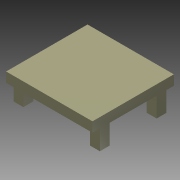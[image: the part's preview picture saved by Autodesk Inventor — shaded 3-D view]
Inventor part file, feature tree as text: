
AUTODESK INVENTOR PART (.ipt)
format: ipt  version: 2015 (Build 190159000, 159)  size: 480,256 bytes
history: native  units: in
note: dims shown in document units (in); Inventor stores cm internally (conversion verified against a paired STEP export)
features: thread x34, other x13, sketch x10, plane x6, projected_geometry x6, extrude x5, hole x4, mirror x3, pattern_circular x1, boolean_combine x1
ambient origin geometry x8: Origin, YZ Plane, XZ Plane, XY Plane, X Axis, Y Axis, Z Axis, Center Point
bodies: Solid6 (feature_tree)
feature tree (83):
  other  "board_with_hole_pipes.ipt"
  other  "Layout with const "
  plane  "Work Plane1"
  extrude  "Extrusion1"  Depth=18.0in
  extrude  "Extrusion2"  Depth=24.0in
  hole  "Hole1"  [1 undecoded]
  thread  "Thread1"  [1 undecoded]
  pattern_circular  "Circular Pattern1"  [2 undecoded]
  plane  "Work Plane3"
  hole  "Hole2"  [1 undecoded]
  thread  "Thread2"  [1 undecoded]
  thread  "Thread3"  [1 undecoded]
  thread  "Thread4"  [1 undecoded]
  thread  "Thread5"  [1 undecoded]
  thread  "Thread6"  [1 undecoded]
  thread  "Thread7"  [1 undecoded]
  mirror  "Mirror1"
  mirror  "Mirror2"
  mirror  "Mirror3"
  plane  "Work Plane4"
  extrude  "Extrusion3"  Depth=1.0in
  thread  "Thread8"  [1 undecoded]
  thread  "Thread9"  [1 undecoded]
  thread  "Thread10"  [1 undecoded]
  thread  "Thread11"  [1 undecoded]
  thread  "Thread12"  [1 undecoded]
  thread  "Thread13"  [1 undecoded]
  thread  "Thread14"  [1 undecoded]
  thread  "Thread15"  [1 undecoded]
  thread  "Thread16"  [1 undecoded]
  thread  "Thread17"  [1 undecoded]
  thread  "Thread18"  [1 undecoded]
  thread  "Thread19"  [1 undecoded]
  thread  "Thread20"  [1 undecoded]
  thread  "Thread21"  [1 undecoded]
  thread  "Thread22"  [1 undecoded]
  thread  "Thread23"  [1 undecoded]
  thread  "Thread24"  [1 undecoded]
  thread  "Thread25"  [1 undecoded]
  extrude  "Extrusion4"  Depth=1.0in TaperAngle=0.0deg
  plane  "Work Plane7"
  extrude  "Extrusion5"  Depth=1.0in TaperAngle=0.0deg
  boolean_combine  "Combine1"
  plane  "Work Plane8"
  plane  "Work Plane9"
  hole  "Hole3"  [1 undecoded]
  hole  "Hole4"  [1 undecoded]
  thread  "Thread26"  [1 undecoded]
  thread  "Thread27"  [1 undecoded]
  thread  "Thread28"  [1 undecoded]
  thread  "Thread29"  [1 undecoded]
  thread  "Thread34"  [1 undecoded]
  thread  "Thread35"  [1 undecoded]
  thread  "Thread36"  [1 undecoded]
  thread  "Thread37"  [1 undecoded]
  thread  "Thread38"  [1 undecoded]
  other  "Solid1::board_with_hole_pipes.ipt"
  other  "TaggingFeature1"
  sketch  "Sketch3"  dims[d0=0.1969in d1=18.0in]
  sketch  "Sketch4"  dims[d2=24.0in d3=23.5in]
  other  "legFL"
  sketch  "Sketch5"  dims[d4=17.5in d5=5.5in d6=1.5in]
  sketch  "Sketch6"  dims[d9=5.5in]
  sketch  "Sketch7"  dims[d10=1.5in]
  other  "Pattern of legFL:1"
  other  "legFR"
  other  "Pattern of legFL:2"
  other  "legBR"
  other  "Pattern of legFR:3"
  other  "legBL"
  sketch  "Sketch8"  dims[d11=5.5in]
  projected_geometry  "Projected Loop2"
  sketch  "Sketch10"  dims[d12=1.5in]
  sketch  "Sketch11"  dims[d15=4.0in]
  other  "miniplat"
  sketch  "Sketch12"  dims[d18=5.5in]
  projected_geometry  "Projected Loop3"
  projected_geometry  "Projected Loop4"
  projected_geometry  "Projected Loop5"
  projected_geometry  "Projected Loop6"
  projected_geometry  "Projected Loop7"
  sketch  "Sketch13"  dims[d19=1.5in d22=5.0in d23=3.0in d24=5.0in d25=3.0in d26=3.0in d27=3.0in d28=3.0in d29=5.0in d30=4.0in d31=3.5in d32=0.5in d33=1.0in d34=0.0in d35=0.0in d36=5.0in d37=0.5in d38=0.0in d39=0.25in d40=0.75in d41=0.375in d42=0.25in d43=0.5635in d44=1.8125in d45=0.8108in d46=1.0in d47=0.0in d48=2.3622in d49=360.0deg d52=0.25in d53=0.75in d54=0.375in d55=0.25in d56=0.5635in d57=1.8125in d58=0.8108in d59=1.0in d60=0.0in d61=1.0in d62=0.0in d63=1.0in d64=0.0in d65=1.0in d66=0.0in d67=1.0in d68=0.0in d69=1.0in d70=0.0in d71=3.475in d72=0.0in d73=1.0in d74=0.0in d75=1.0in d76=0.0in d77=1.0in d78=0.0in d79=1.0in d80=0.0in d81=1.0in d82=0.0in d83=1.0in d84=0.0in d85=1.0in d86=0.0in d87=1.0in d88=0.0in d89=1.0in d90=0.0in d91=1.0in d92=0.0in d93=1.0in d94=0.0in d95=1.0in d96=0.0in d97=1.0in d98=0.0in d99=1.0in d100=0.0in d101=1.0in d102=0.0in d103=1.0in d104=0.0in d105=1.0in d106=0.0in d107=1.0in d108=0.0in d109=1.0in d110=1.0in d111=1.0in d112=1.0in d113=1.0in d114=1.0in d115=2.0in d116=0.0in d117=1.0in d118=0.0in d119=0.5in d120=0.5in d121=0.5in d122=0.5in d123=0.25in d124=0.75in d125=0.375in d126=0.25in d127=0.5635in d128=2.0in d129=0.0in d130=0.5in d131=0.75in d132=0.375in d133=0.25in d134=0.5635in d135=2.0in d136=0.8108in d137=1.0in d138=0.0in d139=1.0in d140=0.0in d141=1.0in d142=0.0in d143=1.0in d144=0.0in d156=1.0in d157=0.0in d158=1.0in d159=0.0in d160=1.0in d161=0.0in d162=1.0in d163=0.0in d164=1.0in d165=0.0in]
  other  "platform"
note: 40 required parameter values undecoded (feature->parameter linkage not recoverable at this tier; creation-order binding heuristic only, values carry confidence <= 0.55)
